# Revit family: Tavolo REA
name_source: partatom
category: Modelli generici
revit_build: Autodesk Revit 2018 (Build: 20170223_1515(x64)
units: mm (PartAtom-declared; Revit-internal decimal feet)

## family parameters
Basato su piano di lavoro = No
Condiviso = No
Punto di calcolo locali = No
Può ospitare armatura = No
Quota connettore circolare = Usa diametro
Sempre verticale = Sì
Taglio con vuoti quando caricato = No
Tipo di parte = Normale

## types (3) — shared parameters
BIM Name = REA
BIM Object Type = TAVOLI - TABLES
Code = 0PAAR169
Descrizione Tecnica Famiglia = "Tavolo mod. “REA” dotato di un corpo principale monolitico con colonna rastremata al centro. Il tavolo è suggerito in associazione alle sedute tipo idra, sedute monolitiche singole."
Designer = BELLITALIA DESIGN
Dimensions = 713 mm X 713 mm X 752 mm
Family Name = REA
Fissaggio = Appoggio
Fixings = Freestanding
IFC = Furnishings
MASTERFORMAT 2014 (DESCRIPTION/CODE) = Seat and Table Assemblies / 12 68 00
OMNICLASS (DESCRIPTION/CODE) = Elements (including designed elements) / 21-00 00 00
Technical Description Family = "table mod. “REA” equipped with a main body monolithic with central tapered column. The table is suggested in association with hydra-type sessions, sessions single monolithic."
UNICLASS 1.4 (DESCRIPTION/CODE) = Street and site tables / Pr_40_30_30_86
UNICLASS 2.0 (DESCRIPTION/CODE) = Street And Site Tables / Pr_40_30_21_86
UNIFORMAT II (DESCRIPTION/CODE) = Furnishings / E20
UNSPSC CATEGORY (CODE) = 231522
URL Eng = https://www.bellitalia.net
URL Ita = https://www.bellitalia.net
Weight ( kg) = 180 Kg

## per-type parameters (varying)
| type | Descrizione Tecnica per Codice | MATERIALE TAVOLO | Materiale Principale | Materiale Secondario | Primary Material | Secondary Material | Technical Description for Article |
| 0PAAR169 - GRANITO | TAVOLO REA IN GRANITO (COLORE A SCELTA) SABBIATO CON PIANO SUPERIORE SPAZZOLATOVERNICIATURA ANTI-DEGRADO | GRANITO | Granito Bianco | Granito Ricostituito | Reconstituted White Granite | Reconstituted Granite | REA TABLE IN GRANITO (COLOR TO BE CHOSEN) SANDBLASTED WITH  BRUSHED UPPER SURFACE ANTI-DECAY VARNISH |
| 0PAAR169 - PIETRE PREZIOSE | TAVOLO REA IN PIETRE PREZIOSE (COLORE A SCELTA ECCETTO VERDE ALPI) SABBIATO CON PIANO SUPERIORE SPAZZOLATOVERNICIATURA ANTI-DEGRADO | PIETRE PREZIOSE | Pietre Preziose Ricostituite Bianco Carrara | Pietre Preziose Ricostituite | Reconstituted Precious Stones Bianco Carrara | Reconstituted Precious Stones | REA TABLE IN PRECIOUS STONES (COLOR TO BE CHOSEN EXCEPT GREEN  ALPS) SANDBLASTED WITH BRUSHED UPPER SURFACE ANTI-DECAY VARNISH |
| 0PAAR169 - VERDE ALPI | TAVOLO REA IN VERDE ALPI SABBIATO CON PIANO SUPERIORE SPAZZOLATOVERNICIATURA ANTI-DEGRADO | VERDE ALPI | Pietre Preziose Ricostituite Verde Alpi | Pietre Preziose Ricostituite | Reconstituted Precious Stones Verde Alpi | Reconstituted Precious Stones | REA TABLE IN GREEN ALPS SANDBLASTED WITH BRUSHED UPPER SURFACE  ANTI-DECAY VARNISH |
